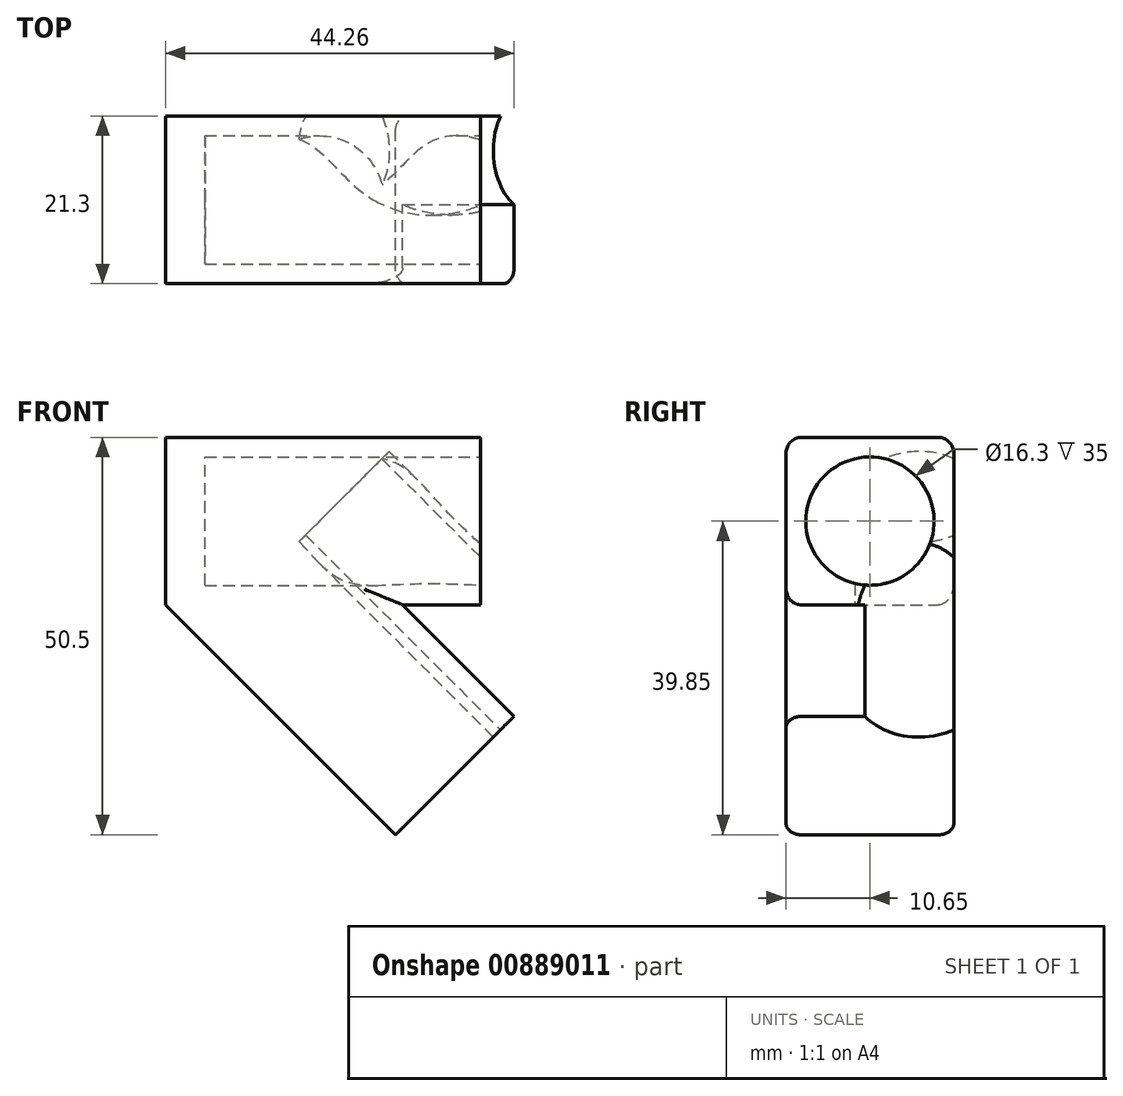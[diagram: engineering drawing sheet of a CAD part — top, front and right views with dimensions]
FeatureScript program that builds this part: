
annotation { "Feature Type Name" : "Feature", "Feature Type Description" : "" }
export const myFeature = defineFeature(function(context is Context, id is Id, definition is map)
    precondition{}
    {
        {
            var Q0;
            Q0=qCreatedBy(makeId("Front.planeOp"),FACE);
            var sketch = newSketch(context, id + "F0", { "sketchPlane" : qUnion([Q0])});
            skLineSegment(sketch, "E0", {"start": v(0, 0) * mm, "end": v(40, 0) * mm});
            skLineSegment(sketch, "E1", {"start": v(40, 0) * mm, "end": v(40, -21.3) * mm});
            skLineSegment(sketch, "E2", {"start": v(40, -21.3) * mm, "end": v(30.12, -21.3) * mm});
            skLineSegment(sketch, "E3", {"start": v(30.12, -21.3) * mm, "end": v(44.26, -35.44) * mm});
            skLineSegment(sketch, "E4", {"start": v(44.26, -35.44) * mm, "end": v(29.2, -50.5) * mm});
            skLineSegment(sketch, "E5", {"start": v(29.2, -50.5) * mm, "end": v(0, -21.3) * mm});
            skLineSegment(sketch, "E6", {"start": v(0, -21.3) * mm, "end": v(0, 0) * mm});
            skLineSegment(sketch, "E7", {"start": v(40, -2.5) * mm, "end": v(2.5, -2.5) * mm});
            skLineSegment(sketch, "E8", {"start": v(2.5, -2.5) * mm, "end": v(2.5, -20.26) * mm});
            skLineSegment(sketch, "E9", {"start": v(2.5, -20.26) * mm, "end": v(30.97, -48.74) * mm});
            skLineSegment(sketch, "E10", {"start": v(30.97, -48.74) * mm, "end": v(42.5, -37.2) * mm});
            skLineSegment(sketch, "E11", {"start": v(42.5, -37.2) * mm, "end": v(24.09, -18.8) * mm});
            skLineSegment(sketch, "E12", {"start": v(24.09, -18.8) * mm, "end": v(40, -18.8) * mm});
            skSolve(sketch);
        }
        {
            var Q0;
            {var subQ3=sQuery(id+"F0.wireOp",EDGE,"E2");Q0=makeQuery(id+"F0.imprint","IMPRINT",FACE,{"disambiguationData":[TD([[makeQuery(id+"F0.imprint","IMPRINT",EDGE,{"derivedFrom":subQ3}),-1.0]])]});}
            var Q1;
            {var subQ0=sQuery(id+"F0.wireOp",EDGE,"E7");Q1=makeQuery(id+"F0.imprint","IMPRINT",FACE,{"disambiguationData":[TD([[makeQuery(id+"F0.imprint","IMPRINT",EDGE,{"derivedFrom":subQ0}),1.0]])]});}
            var Q2;
            {var subQ4=sQuery(id+"F0.wireOp",EDGE,"E0");Q2=makeQuery(id+"F0.imprint","IMPRINT",FACE,{"disambiguationData":[TD([[makeQuery(id+"F0.imprint","IMPRINT",EDGE,{"derivedFrom":subQ4}),-1.0]])]});}
            extrude(context, id + "F1", {"entities" : qUnion([Q0, Q1, Q2]), "depth" : 21.3 * mm, "offsetDistance" : 25 * mm});
        }
        {
            var Q0;
            Q0=makeQuery(id+"F1.opExtrude","SWEPT_FACE",FACE,{"disambiguationData":[OSD([sQuery(id+"F0.wireOp",EDGE,"E1")])]});
            var sketch = newSketch(context, id + "F2", { "sketchPlane" : qUnion([Q0])});
            skCircle(sketch, "E13", {"center": v(-10.65, -10.65) * mm, "radius": 8.15 * mm});
            skSolve(sketch);
        }
        {
            var Q0;
            Q0=makeQuery(id+"F1.opExtrude","SWEPT_FACE",FACE,{"disambiguationData":[OSD([sQuery(id+"F0.wireOp",EDGE,"E4"),sQuery(id+"F0.wireOp",EDGE,"E10")])]});
            var sketch = newSketch(context, id + "F3", { "sketchPlane" : qUnion([Q0])});
            skCircle(sketch, "E14", {"center": v(-4.41, 10.65) * mm, "radius": 8.15 * mm});
            skSolve(sketch);
        }
        {
            var Q0;
            Q0=makeQuery(id+"F3.imprint","IMPRINT",FACE,{"disambiguationData":[TD([[makeQuery(id+"F3.imprint","IMPRINT",EDGE,{"derivedFrom":sQuery(id+"F3.wireOp",EDGE,"E14")}),1.0]])]});
            extrude(context, id + "F4", {"entities" : qUnion([Q0]), "operationType" : NewBodyOperationType.REMOVE, "oppositeDirection" : true, "depth" : 35 * mm, "offsetDistance" : 25 * mm});
        }
        {
            var Q0;
            Q0=makeQuery(id+"F2.imprint","IMPRINT",FACE,{"disambiguationData":[TD([[makeQuery(id+"F2.imprint","IMPRINT",EDGE,{"derivedFrom":sQuery(id+"F2.wireOp",EDGE,"E13")}),1.0]])]});
            extrude(context, id + "F5", {"entities" : qUnion([Q0]), "operationType" : NewBodyOperationType.REMOVE, "oppositeDirection" : true, "depth" : 35 * mm, "offsetDistance" : 25 * mm});
        }
        {
            var Q0;
            Q0=makeQuery(id+"F1.opExtrude","CAP_EDGE",EDGE,{"disambiguationData":[OSD([sQuery(id+"F0.wireOp",EDGE,"E0")])],"isStart":true});
            var Q1;
            Q1=makeQuery(id+"F1.opExtrude","CAP_EDGE",EDGE,{"disambiguationData":[OSD([sQuery(id+"F0.wireOp",EDGE,"E0")])],"isStart":false});
            var Q2;
            Q2=makeQuery(id+"F1.opExtrude","CAP_EDGE",EDGE,{"disambiguationData":[OSD([sQuery(id+"F0.wireOp",EDGE,"E5")])],"isStart":false});
            var Q3;
            Q3=makeQuery(id+"F1.opExtrude","CAP_EDGE",EDGE,{"disambiguationData":[OSD([sQuery(id+"F0.wireOp",EDGE,"E5")])],"isStart":true});
            var Q4;
            Q4=makeQuery(id+"F1.opExtrude","CAP_EDGE",EDGE,{"disambiguationData":[OSD([sQuery(id+"F0.wireOp",EDGE,"E3")])],"isStart":false});
            var Q5;
            Q5=makeQuery(id+"F1.opExtrude","CAP_EDGE",EDGE,{"disambiguationData":[OSD([sQuery(id+"F0.wireOp",EDGE,"E3")])],"isStart":true});
            var Q6;
            Q6=makeQuery(id+"F1.opExtrude","CAP_EDGE",EDGE,{"disambiguationData":[OSD([sQuery(id+"F0.wireOp",EDGE,"E2")])],"isStart":true});
            var Q7;
            Q7=makeQuery(id+"F1.opExtrude","CAP_EDGE",EDGE,{"disambiguationData":[OSD([sQuery(id+"F0.wireOp",EDGE,"E2")])],"isStart":false});
            fillet(context, id + "F6", {"entities" : qUnion([Q0, Q1, Q2, Q3, Q4, Q5, Q6, Q7]), "radius" : 2 * mm, "tangentPropagation" : true, "allowEdgeOverflow" : false});
        }
    });
